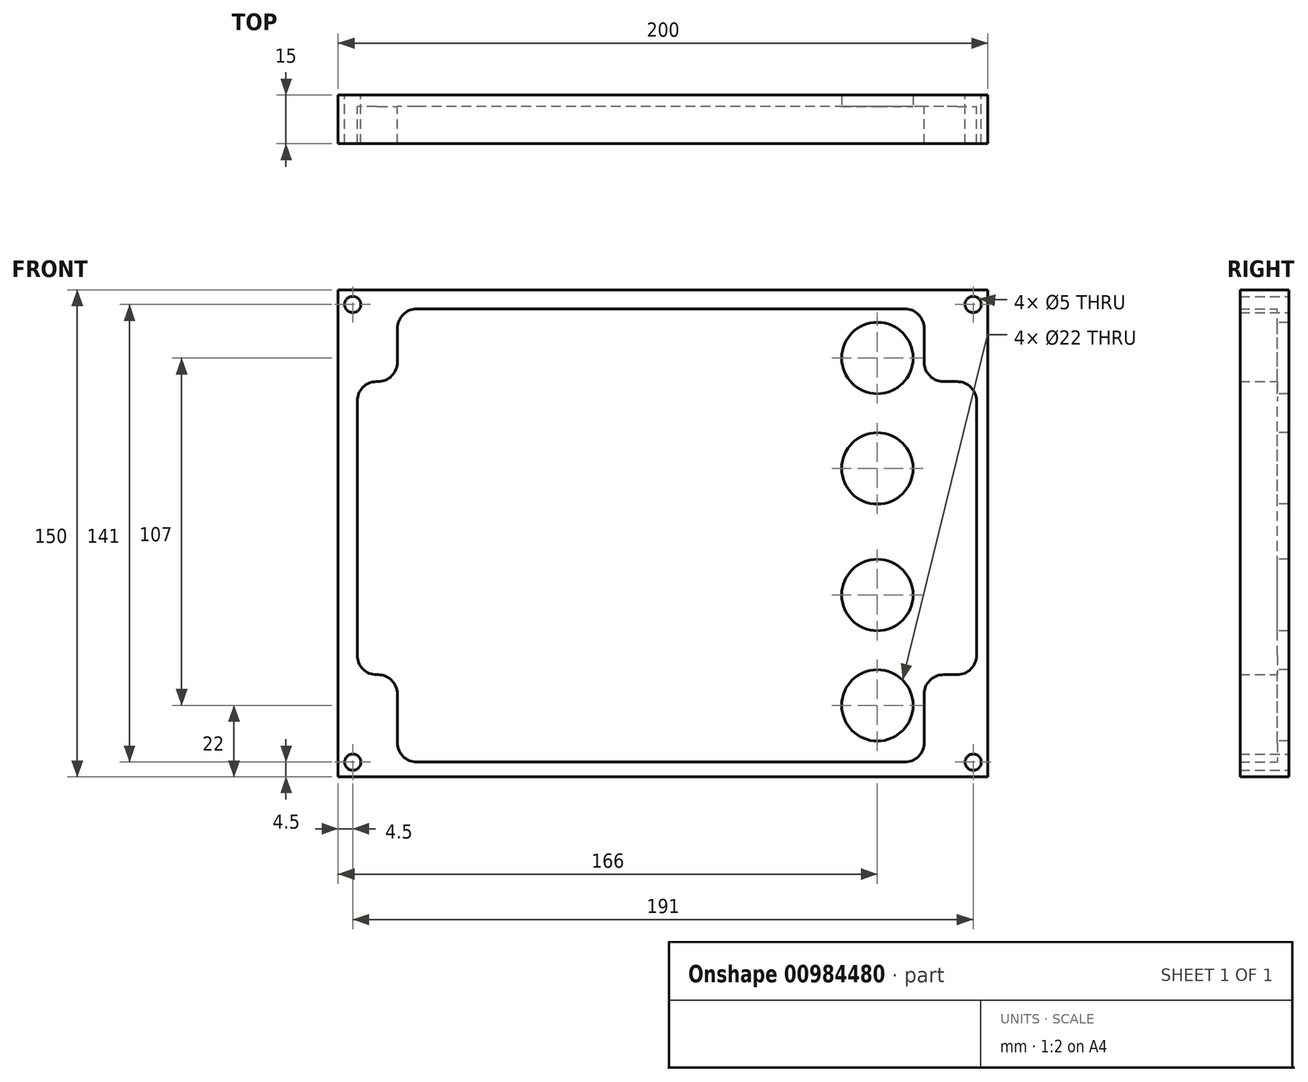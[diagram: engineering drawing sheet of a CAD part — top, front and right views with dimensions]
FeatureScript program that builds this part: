
annotation { "Feature Type Name" : "Feature", "Feature Type Description" : "" }
export const myFeature = defineFeature(function(context is Context, id is Id, definition is map)
    precondition{}
    {
        {
            var Q0;
            Q0=qCreatedBy(makeId("Front.planeOp"),FACE);
            var sketch = newSketch(context, id + "F0", { "sketchPlane" : qUnion([Q0])});
            skLineSegment(sketch, "E0.bottom", {"start": v(-186, 145.5) * mm, "end": v(14, 145.5) * mm});
            skLineSegment(sketch, "E0.top", {"start": v(-186, -4.5) * mm, "end": v(14, -4.5) * mm});
            skLineSegment(sketch, "E0.left", {"start": v(-186, 145.5) * mm, "end": v(-186, -4.5) * mm});
            skLineSegment(sketch, "E0.right", {"start": v(14, 145.5) * mm, "end": v(14, -4.5) * mm});
            skCircle(sketch, "E1", {"center": v(-181.5, 141) * mm, "radius": 2.5 * mm});
            skCircle(sketch, "E2", {"center": v(-181.5, 0) * mm, "radius": 2.5 * mm});
            skCircle(sketch, "E3", {"center": v(9.5, 0) * mm, "radius": 2.5 * mm});
            skCircle(sketch, "E4", {"center": v(9.5, 141) * mm, "radius": 2.5 * mm});
            skLineSegment(sketch, "E5.bottom", {"start": v(-172, 145.5) * mm, "end": v(-186, 145.5) * mm});
            skLineSegment(sketch, "E5.top", {"start": v(-172, 122) * mm, "end": v(-186, 122) * mm});
            skLineSegment(sketch, "E5.left", {"start": v(-172, 145.5) * mm, "end": v(-172, 122) * mm});
            skLineSegment(sketch, "E5.right", {"start": v(-186, 145.5) * mm, "end": v(-186, 122) * mm});
            skLineSegment(sketch, "E6.bottom", {"start": v(0, 145.5) * mm, "end": v(14, 145.5) * mm});
            skLineSegment(sketch, "E6.top", {"start": v(0, 122) * mm, "end": v(14, 122) * mm});
            skLineSegment(sketch, "E6.left", {"start": v(0, 145.5) * mm, "end": v(0, 122) * mm});
            skLineSegment(sketch, "E6.right", {"start": v(14, 145.5) * mm, "end": v(14, 122) * mm});
            skLineSegment(sketch, "E7.bottom", {"start": v(14, 19) * mm, "end": v(0, 19) * mm});
            skLineSegment(sketch, "E7.top", {"start": v(14, -4.5) * mm, "end": v(0, -4.5) * mm});
            skLineSegment(sketch, "E7.left", {"start": v(14, 19) * mm, "end": v(14, -4.5) * mm});
            skLineSegment(sketch, "E7.right", {"start": v(0, 19) * mm, "end": v(0, -4.5) * mm});
            skLineSegment(sketch, "E8.bottom", {"start": v(-186, 19) * mm, "end": v(-172, 19) * mm});
            skLineSegment(sketch, "E8.top", {"start": v(-186, -4.5) * mm, "end": v(-172, -4.5) * mm});
            skLineSegment(sketch, "E8.left", {"start": v(-186, 19) * mm, "end": v(-186, -4.5) * mm});
            skLineSegment(sketch, "E8.right", {"start": v(-172, 19) * mm, "end": v(-172, -4.5) * mm});
            skLineSegment(sketch, "E9", {"start": v(-5.6, 139.66) * mm, "end": v(-167.76, 139.66) * mm});
            skLineSegment(sketch, "E10", {"start": v(-167.76, 139.66) * mm, "end": v(-167.76, 117.24) * mm});
            skLineSegment(sketch, "E11", {"start": v(-167.76, 117.24) * mm, "end": v(-180.13, 117.24) * mm});
            skLineSegment(sketch, "E12", {"start": v(-180.13, 117.24) * mm, "end": v(-180.13, 26.94) * mm});
            skLineSegment(sketch, "E13", {"start": v(-180.13, 26.94) * mm, "end": v(-167.76, 26.94) * mm});
            skLineSegment(sketch, "E14", {"start": v(-167.76, 26.94) * mm, "end": v(-167.76, 0) * mm});
            skLineSegment(sketch, "E15", {"start": v(-167.76, 0) * mm, "end": v(-5.6, 0) * mm});
            skLineSegment(sketch, "E16", {"start": v(-5.6, 0) * mm, "end": v(-5.6, 26.94) * mm});
            skLineSegment(sketch, "E17", {"start": v(-5.6, 26.94) * mm, "end": v(10.54, 26.94) * mm});
            skLineSegment(sketch, "E18", {"start": v(10.54, 26.94) * mm, "end": v(10.54, 117.24) * mm});
            skLineSegment(sketch, "E19", {"start": v(10.54, 117.24) * mm, "end": v(-5.6, 117.24) * mm});
            skLineSegment(sketch, "E20", {"start": v(-5.6, 117.24) * mm, "end": v(-5.6, 139.66) * mm});
            skSolve(sketch);
        }
        {
            var Q0;
            Q0=qSketchRegion(id+"F0",true);
            extrude(context, id + "F1", {"entities" : qUnion([Q0]), "depth" : 15 * mm, "offsetDistance" : 25 * mm});
        }
        {
            var Q0;
            Q0=makeQuery(id+"F0.imprint","IMPRINT",FACE,{"disambiguationData":[TD([[makeQuery(id+"F0.imprint","IMPRINT",EDGE,{"derivedFrom":sQuery(id+"F0.wireOp",EDGE,"E9")}),1.0]])]});
            extrude(context, id + "F2", {"entities" : qUnion([Q0]), "operationType" : NewBodyOperationType.ADD, "depth" : 3.5 * mm, "offsetDistance" : 25 * mm});
        }
        {
            var Q0;
            Q0=makeQuery(id+"F1.opExtrude","SWEPT_EDGE",EDGE,{"disambiguationData":[OSD([sQuery(id+"F0.wireOp",EDGE,"E5.bottom"),sQuery(id+"F0.wireOp",EDGE,"E5.right")])]});
            var Q1;
            Q1=makeQuery(id+"F1.opExtrude","SWEPT_EDGE",EDGE,{"disambiguationData":[OSD([sQuery(id+"F0.wireOp",EDGE,"E8.top"),sQuery(id+"F0.wireOp",EDGE,"E8.left")])]});
            var Q2;
            Q2=makeQuery(id+"F1.opExtrude","SWEPT_EDGE",EDGE,{"disambiguationData":[OSD([sQuery(id+"F0.wireOp",EDGE,"E7.top"),sQuery(id+"F0.wireOp",EDGE,"E7.left")])]});
            var Q3;
            Q3=makeQuery(id+"F1.opExtrude","SWEPT_EDGE",EDGE,{"disambiguationData":[OSD([sQuery(id+"F0.wireOp",EDGE,"E6.bottom"),sQuery(id+"F0.wireOp",EDGE,"E6.right")])]});
            var Q4;
            Q4=makeQuery(id+"F1.opExtrude","SWEPT_EDGE",EDGE,{"disambiguationData":[OSD([sQuery(id+"F0.wireOp",EDGE,"E12"),sQuery(id+"F0.wireOp",EDGE,"E13")])]});
            var Q5;
            Q5=makeQuery(id+"F1.opExtrude","SWEPT_EDGE",EDGE,{"disambiguationData":[OSD([sQuery(id+"F0.wireOp",EDGE,"E13"),sQuery(id+"F0.wireOp",EDGE,"E14")])]});
            var Q6;
            Q6=makeQuery(id+"F1.opExtrude","SWEPT_EDGE",EDGE,{"disambiguationData":[OSD([sQuery(id+"F0.wireOp",EDGE,"E14"),sQuery(id+"F0.wireOp",EDGE,"E15")])]});
            var Q7;
            Q7=makeQuery(id+"F1.opExtrude","SWEPT_EDGE",EDGE,{"disambiguationData":[OSD([sQuery(id+"F0.wireOp",EDGE,"E15"),sQuery(id+"F0.wireOp",EDGE,"E16")])]});
            var Q8;
            Q8=makeQuery(id+"F1.opExtrude","SWEPT_EDGE",EDGE,{"disambiguationData":[OSD([sQuery(id+"F0.wireOp",EDGE,"E16"),sQuery(id+"F0.wireOp",EDGE,"E17")])]});
            var Q9;
            Q9=makeQuery(id+"F1.opExtrude","SWEPT_EDGE",EDGE,{"disambiguationData":[OSD([sQuery(id+"F0.wireOp",EDGE,"E17"),sQuery(id+"F0.wireOp",EDGE,"E18")])]});
            var Q10;
            Q10=makeQuery(id+"F1.opExtrude","SWEPT_EDGE",EDGE,{"disambiguationData":[OSD([sQuery(id+"F0.wireOp",EDGE,"E11"),sQuery(id+"F0.wireOp",EDGE,"E12")])]});
            var Q11;
            Q11=makeQuery(id+"F1.opExtrude","SWEPT_EDGE",EDGE,{"disambiguationData":[OSD([sQuery(id+"F0.wireOp",EDGE,"E10"),sQuery(id+"F0.wireOp",EDGE,"E11")])]});
            var Q12;
            Q12=makeQuery(id+"F1.opExtrude","SWEPT_EDGE",EDGE,{"disambiguationData":[OSD([sQuery(id+"F0.wireOp",EDGE,"E9"),sQuery(id+"F0.wireOp",EDGE,"E10")])]});
            var Q13;
            Q13=makeQuery(id+"F1.opExtrude","SWEPT_EDGE",EDGE,{"disambiguationData":[OSD([sQuery(id+"F0.wireOp",EDGE,"E18"),sQuery(id+"F0.wireOp",EDGE,"E19")])]});
            var Q14;
            Q14=makeQuery(id+"F1.opExtrude","SWEPT_EDGE",EDGE,{"disambiguationData":[OSD([sQuery(id+"F0.wireOp",EDGE,"E19"),sQuery(id+"F0.wireOp",EDGE,"E20")])]});
            var Q15;
            Q15=makeQuery(id+"F1.opExtrude","SWEPT_EDGE",EDGE,{"disambiguationData":[OSD([sQuery(id+"F0.wireOp",EDGE,"E9"),sQuery(id+"F0.wireOp",EDGE,"E20")])]});
            fillet(context, id + "F3", {"entities" : qUnion([Q0, Q1, Q2, Q3, Q4, Q5, Q6, Q7, Q8, Q9, Q10, Q11, Q12, Q13, Q14, Q15]), "radius" : 6 * mm, "tangentPropagation" : true, "allowEdgeOverflow" : false});
        }
        {
            var Q0;
            Q0=makeQuery(id+"F2.opExtrude","CAP_FACE",FACE,{"disambiguationData":[OSD([sQuery(id+"F0.wireOp",EDGE,"E9"),sQuery(id+"F0.wireOp",EDGE,"E10"),sQuery(id+"F0.wireOp",EDGE,"E11"),sQuery(id+"F0.wireOp",EDGE,"E12"),sQuery(id+"F0.wireOp",EDGE,"E13"),sQuery(id+"F0.wireOp",EDGE,"E14"),sQuery(id+"F0.wireOp",EDGE,"E15"),sQuery(id+"F0.wireOp",EDGE,"E16"),sQuery(id+"F0.wireOp",EDGE,"E17"),sQuery(id+"F0.wireOp",EDGE,"E18"),sQuery(id+"F0.wireOp",EDGE,"E19"),sQuery(id+"F0.wireOp",EDGE,"E20")])],"isStart":false});
            var sketch = newSketch(context, id + "F4", { "sketchPlane" : qUnion([Q0])});
            skCircle(sketch, "E21", {"center": v(-20, 124.5) * mm, "radius": 11 * mm});
            skCircle(sketch, "E22", {"center": v(-20, 90.5) * mm, "radius": 11 * mm});
            skCircle(sketch, "E23", {"center": v(-20, 51.5) * mm, "radius": 11 * mm});
            skCircle(sketch, "E24", {"center": v(-20, 17.5) * mm, "radius": 11 * mm});
            skSolve(sketch);
        }
        {
            var Q0;
            Q0 = qSketchRegion(id + "F4", true);
            extrude(context, id + "F5", {"entities" : qUnion([Q0]), "operationType" : NewBodyOperationType.REMOVE, "oppositeDirection" : true, "depth" : 25 * mm, "offsetDistance" : 25 * mm});
        }
    });
